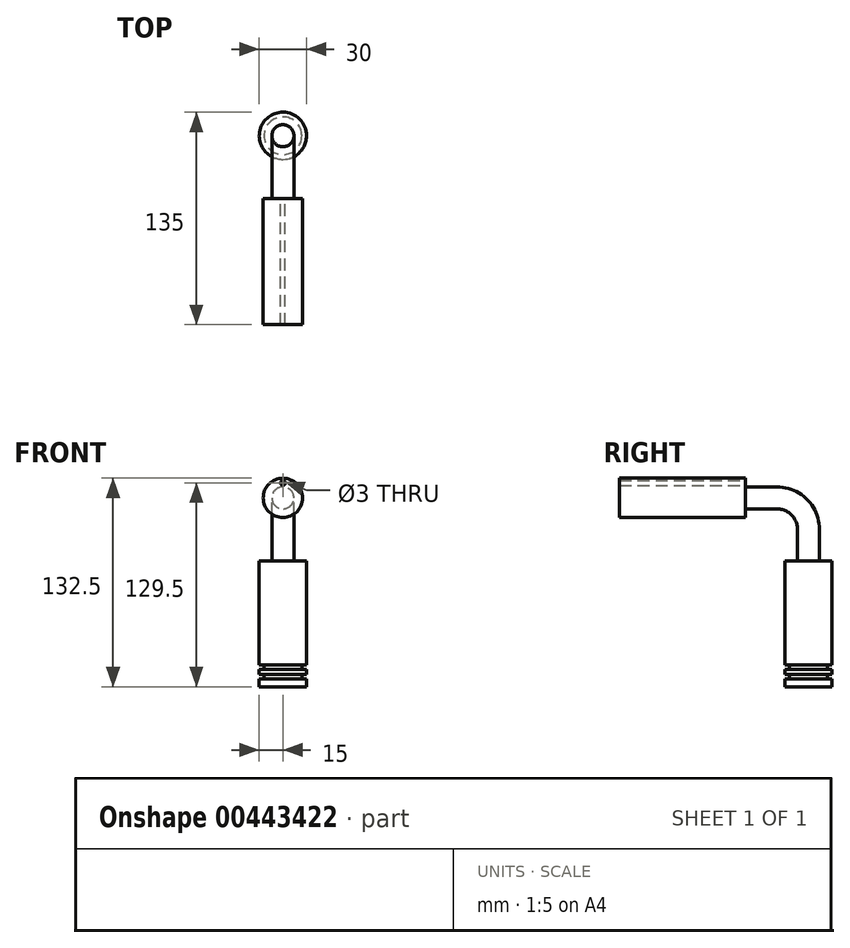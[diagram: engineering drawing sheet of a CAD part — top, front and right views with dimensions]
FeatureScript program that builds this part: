
annotation { "Feature Type Name" : "Feature", "Feature Type Description" : "" }
export const myFeature = defineFeature(function(context is Context, id is Id, definition is map)
    precondition{}
    {
        {
            var Q0;
            Q0=qCreatedBy(makeId("Front.planeOp"),FACE);
            var sketch = newSketch(context, id + "F0", { "sketchPlane" : qUnion([Q0])});
            skCircle(sketch, "E0", {"center": v(0, 0) * mm, "radius": 12.5 * mm});
            skSolve(sketch);
        }
        {
            var Q0;
            Q0=makeQuery(id+"F0.imprint","IMPRINT",FACE,{"disambiguationData":[TD([[makeQuery(id+"F0.imprint","IMPRINT",EDGE,{"derivedFrom":sQuery(id+"F0.wireOp",EDGE,"E0")}),1.0]])]});
            extrude(context, id + "F1", {"entities" : qUnion([Q0]), "oppositeDirection" : true, "depth" : 80 * mm});
        }
        {
            var Q0;
            Q0=makeQuery(id+"F1.opExtrude","CAP_FACE",FACE,{"disambiguationData":[OSD([sQuery(id+"F0.wireOp",EDGE,"E0")])],"isStart":false});
            var sketch = newSketch(context, id + "F2", { "sketchPlane" : qUnion([Q0])});
            skCircle(sketch, "E1", {"center": v(0, 0) * mm, "radius": 7 * mm});
            skSolve(sketch);
        }
        {
            var Q0;
            Q0=makeQuery(id+"F2.imprint","IMPRINT",FACE,{"disambiguationData":[TD([[makeQuery(id+"F2.imprint","IMPRINT",EDGE,{"derivedFrom":sQuery(id+"F2.wireOp",EDGE,"E1")}),1.0]])]});
            extrude(context, id + "F3", {"entities" : qUnion([Q0]), "operationType" : NewBodyOperationType.ADD, "depth" : 20 * mm});
        }
        {
            var Q0;
            Q0=qCreatedBy(makeId("Right.planeOp"),FACE);
            var sketch = newSketch(context, id + "F4", { "sketchPlane" : qUnion([Q0])});
            skArc(sketch, "E2", {"start": v(100, 0) * mm, "mid": v(114.14, -5.86) * mm, "end": v(120, -20) * mm});
            skSolve(sketch);
        }
        {
            var Q0;
            Q0=makeQuery(id+"F3.opExtrude","CAP_FACE",FACE,{"disambiguationData":[OSD([sQuery(id+"F2.wireOp",EDGE,"E1")])],"isStart":false});
            var Q1;
            Q1=sQuery(id+"F4.wireOp",EDGE,"E2");
            sweep(context, id + "F5", {"operationType" : NewBodyOperationType.ADD, "profiles" : qUnion([Q0]), "path" : qUnion([Q1])});
        }
        {
            var Q0;
            Q0=makeQuery(id+"F5.opSweep","CAP_FACE",FACE,{"disambiguationData":[OSD([sQuery(id+"F2.wireOp",EDGE,"E1"),sQuery(id+"F4.wireOp",VERTEX,"E2.end")])],"isStart":false});
            extrude(context, id + "F6", {"entities" : qUnion([Q0]), "operationType" : NewBodyOperationType.ADD, "depth" : 20 * mm});
        }
        {
            var Q0;
            Q0=makeQuery(id+"F6.opExtrude","CAP_FACE",FACE,{"disambiguationData":[OSD([sQuery(id+"F2.wireOp",EDGE,"E1"),sQuery(id+"F4.wireOp",VERTEX,"E2.end")])],"isStart":false});
            var sketch = newSketch(context, id + "F7", { "sketchPlane" : qUnion([Q0])});
            skCircle(sketch, "E3", {"center": v(0, -120) * mm, "radius": 15 * mm});
            skSolve(sketch);
        }
        {
            var Q0;
            Q0 = qSketchRegion(id + "F7", true);
            extrude(context, id + "F8", {"entities" : qUnion([Q0]), "operationType" : NewBodyOperationType.ADD, "depth" : 80 * mm});
        }
        {
            var Q0;
            Q0=makeQuery(id+"F1.opExtrude","CAP_FACE",FACE,{"disambiguationData":[OSD([sQuery(id+"F0.wireOp",EDGE,"E0")])],"isStart":false});
            var sketch = newSketch(context, id + "F9", { "sketchPlane" : qUnion([Q0])});
            skCircle(sketch, "E4", {"center": v(0, 9.5) * mm, "radius": 1.5 * mm});
            skSolve(sketch);
        }
        {
            var Q0;
            Q0 = qSketchRegion(id + "F9", true);
            extrude(context, id + "F10", {"entities" : qUnion([Q0]), "operationType" : NewBodyOperationType.REMOVE, "endBound" : BoundingType.THROUGH_ALL, "oppositeDirection" : true, "depth" : 25 * mm});
        }
        {
            var Q0;
            Q0=qCreatedBy(makeId("Right.planeOp"),FACE);
            var sketch = newSketch(context, id + "F11", { "sketchPlane" : qUnion([Q0])});
            skLineSegment(sketch, "E5.bottom", {"start": v(105, -106) * mm, "end": v(108, -106) * mm});
            skLineSegment(sketch, "E5.top", {"start": v(105, -109) * mm, "end": v(108, -109) * mm});
            skLineSegment(sketch, "E5.left", {"start": v(105, -106) * mm, "end": v(105, -109) * mm});
            skLineSegment(sketch, "E5.right", {"start": v(108, -106) * mm, "end": v(108, -109) * mm});
            skLineSegment(sketch, "E6.bottom", {"start": v(105, -112) * mm, "end": v(108, -112) * mm});
            skLineSegment(sketch, "E6.top", {"start": v(105, -115) * mm, "end": v(108, -115) * mm});
            skLineSegment(sketch, "E6.left", {"start": v(105, -112) * mm, "end": v(105, -115) * mm});
            skLineSegment(sketch, "E6.right", {"start": v(108, -112) * mm, "end": v(108, -115) * mm});
            skLineSegment(sketch, "E7.0", {"start": v(135, -120) * mm, "end": v(105, -120) * mm});
            skLineSegment(sketch, "E8", {"start": v(120, -120) * mm, "end": v(120, -83.85) * mm, "construction": true});
            skSolve(sketch);
        }
        {
            var Q0;
            Q0 = qSketchRegion(id + "F11", true);
            var Q1;
            Q1=sQuery(id+"F11.wireOp",EDGE,"E8");
            revolve(context, id + "F12", {"operationType" : NewBodyOperationType.REMOVE, "entities" : qUnion([Q0]), "axis" : qUnion([Q1]), "revolveType" : RevolveType.FULL, "oppositeDirection" : true});
        }
    });
